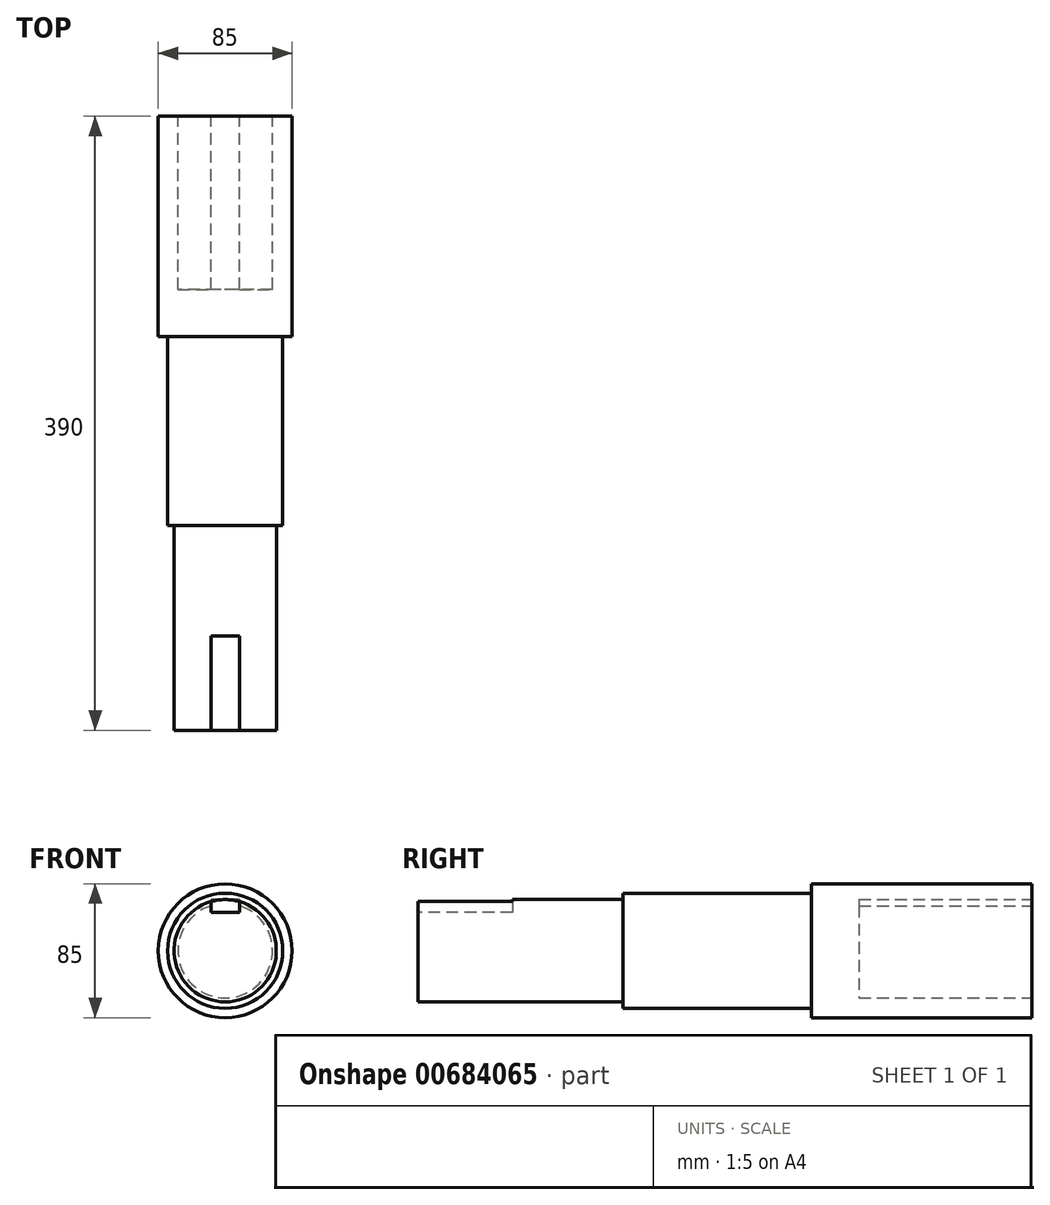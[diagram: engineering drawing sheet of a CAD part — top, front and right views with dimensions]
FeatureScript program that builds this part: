
annotation { "Feature Type Name" : "Feature", "Feature Type Description" : "" }
export const myFeature = defineFeature(function(context is Context, id is Id, definition is map)
    precondition{}
    {
        {
            var Q0;
            Q0=qCreatedBy(makeId("Front.planeOp"),FACE);
            var sketch = newSketch(context, id + "F0", { "sketchPlane" : qUnion([Q0])});
            skCircle(sketch, "E0", {"center": v(0, 0) * mm, "radius": 32.5 * mm});
            skSolve(sketch);
        }
        {
            var Q0;
            Q0 = qSketchRegion(id + "F0", true);
            extrude(context, id + "F1", {"entities" : qUnion([Q0]), "oppositeDirection" : true, "depth" : 100 * mm, "offsetDistance" : 25.4 * mm});
        }
        {
            var Q0;
            Q0=makeQuery(id+"F1.opExtrude","CAP_FACE",FACE,{"disambiguationData":[OSD([sQuery(id+"F0.wireOp",EDGE,"E0")])],"isStart":false});
            var sketch = newSketch(context, id + "F2", { "sketchPlane" : qUnion([Q0])});
            skCircle(sketch, "E1", {"center": v(0, 0) * mm, "radius": 36.59 * mm});
            skSolve(sketch);
        }
        {
            var Q0;
            Q0 = qSketchRegion(id + "F2", true);
            extrude(context, id + "F3", {"entities" : qUnion([Q0]), "operationType" : NewBodyOperationType.ADD, "depth" : 150 * mm, "offsetDistance" : 25.4 * mm});
        }
        {
            var Q0;
            Q0=makeQuery(id+"F3.opExtrude","CAP_FACE",FACE,{"disambiguationData":[OSD([sQuery(id+"F2.wireOp",EDGE,"E1")])],"isStart":false});
            var sketch = newSketch(context, id + "F4", { "sketchPlane" : qUnion([Q0])});
            skCircle(sketch, "E2", {"center": v(0, 0) * mm, "radius": 42.5 * mm});
            skSolve(sketch);
        }
        {
            var Q0;
            Q0 = qSketchRegion(id + "F4", true);
            extrude(context, id + "F5", {"entities" : qUnion([Q0]), "operationType" : NewBodyOperationType.ADD, "depth" : 140 * mm, "offsetDistance" : 25.4 * mm});
        }
        {
            var Q0;
            Q0=makeQuery(id+"F5.opExtrude","CAP_FACE",FACE,{"disambiguationData":[OSD([sQuery(id+"F4.wireOp",EDGE,"E2")])],"isStart":false});
            var sketch = newSketch(context, id + "F6", { "sketchPlane" : qUnion([Q0])});
            skArc(sketch, "E3", {"start": v(-9, 28.62) * mm, "mid": v(0, -30) * mm, "end": v(9, 28.62) * mm});
            skLineSegment(sketch, "E4.bottom", {"start": v(-9, 32.62) * mm, "end": v(9, 32.62) * mm});
            skLineSegment(sketch, "E4.left", {"start": v(-9, 32.62) * mm, "end": v(-9, 28.62) * mm});
            skLineSegment(sketch, "E4.right", {"start": v(9, 32.62) * mm, "end": v(9, 28.62) * mm});
            skPoint(sketch, "E5.startSnap0", {"position": v(0, 28.62) * mm});
            skSolve(sketch);
        }
        {
            var Q0;
            Q0=makeQuery(id+"F6.imprint","IMPRINT",FACE,{"disambiguationData":[TD([[makeQuery(id+"F6.imprint","IMPRINT",EDGE,{"derivedFrom":sQuery(id+"F6.wireOp",EDGE,"E3")}),1.0]])]});
            extrude(context, id + "F7", {"entities" : qUnion([Q0]), "operationType" : NewBodyOperationType.REMOVE, "oppositeDirection" : true, "depth" : 110 * mm, "offsetDistance" : 25.4 * mm});
        }
        {
            var Q0;
            Q0=makeQuery(id+"F1.opExtrude","CAP_FACE",FACE,{"disambiguationData":[OSD([sQuery(id+"F0.wireOp",EDGE,"E0")])],"isStart":true});
            var sketch = newSketch(context, id + "F8", { "sketchPlane" : qUnion([Q0])});
            skLineSegment(sketch, "E6", {"start": v(-9, 31.23) * mm, "end": v(-9, 24.23) * mm});
            skLineSegment(sketch, "E7", {"start": v(-9, 24.23) * mm, "end": v(9, 24.23) * mm});
            skLineSegment(sketch, "E8", {"start": v(9, 24.23) * mm, "end": v(9, 31.23) * mm});
            skArc(sketch, "E9", {"start": v(-9, 31.23) * mm, "mid": v(0, 32.5) * mm, "end": v(9, 31.23) * mm});
            skSolve(sketch);
        }
        {
            var Q0;
            Q0=makeQuery(id+"F8.imprint","IMPRINT",FACE,{"disambiguationData":[TD([[makeQuery(id+"F8.imprint","IMPRINT",EDGE,{"derivedFrom":sQuery(id+"F8.wireOp",EDGE,"E6")}),1.0]])]});
            extrude(context, id + "F9", {"entities" : qUnion([Q0]), "operationType" : NewBodyOperationType.REMOVE, "oppositeDirection" : true, "depth" : 60 * mm, "offsetDistance" : 25.4 * mm});
        }
        {
            var Q0;
            Q0=makeQuery(id+"F3.opExtrude","CAP_FACE",FACE,{"disambiguationData":[OSD([sQuery(id+"F2.wireOp",EDGE,"E1")])],"isStart":true});
            var sketch = newSketch(context, id + "F10", { "sketchPlane" : qUnion([Q0])});
            skCircle(sketch, "E10", {"center": v(0, 0) * mm, "radius": 32.5 * mm});
            skSolve(sketch);
        }
        {
            var Q0;
            Q0=makeQuery(id+"F10.imprint","IMPRINT",FACE,{"disambiguationData":[TD([[makeQuery(id+"F10.imprint","IMPRINT",EDGE,{"derivedFrom":sQuery(id+"F10.wireOp",EDGE,"E10")}),-1.0]])]});
            extrude(context, id + "F11", {"entities" : qUnion([Q0]), "operationType" : NewBodyOperationType.REMOVE, "oppositeDirection" : true, "depth" : 30 * mm, "offsetDistance" : 25.4 * mm});
        }
    });
